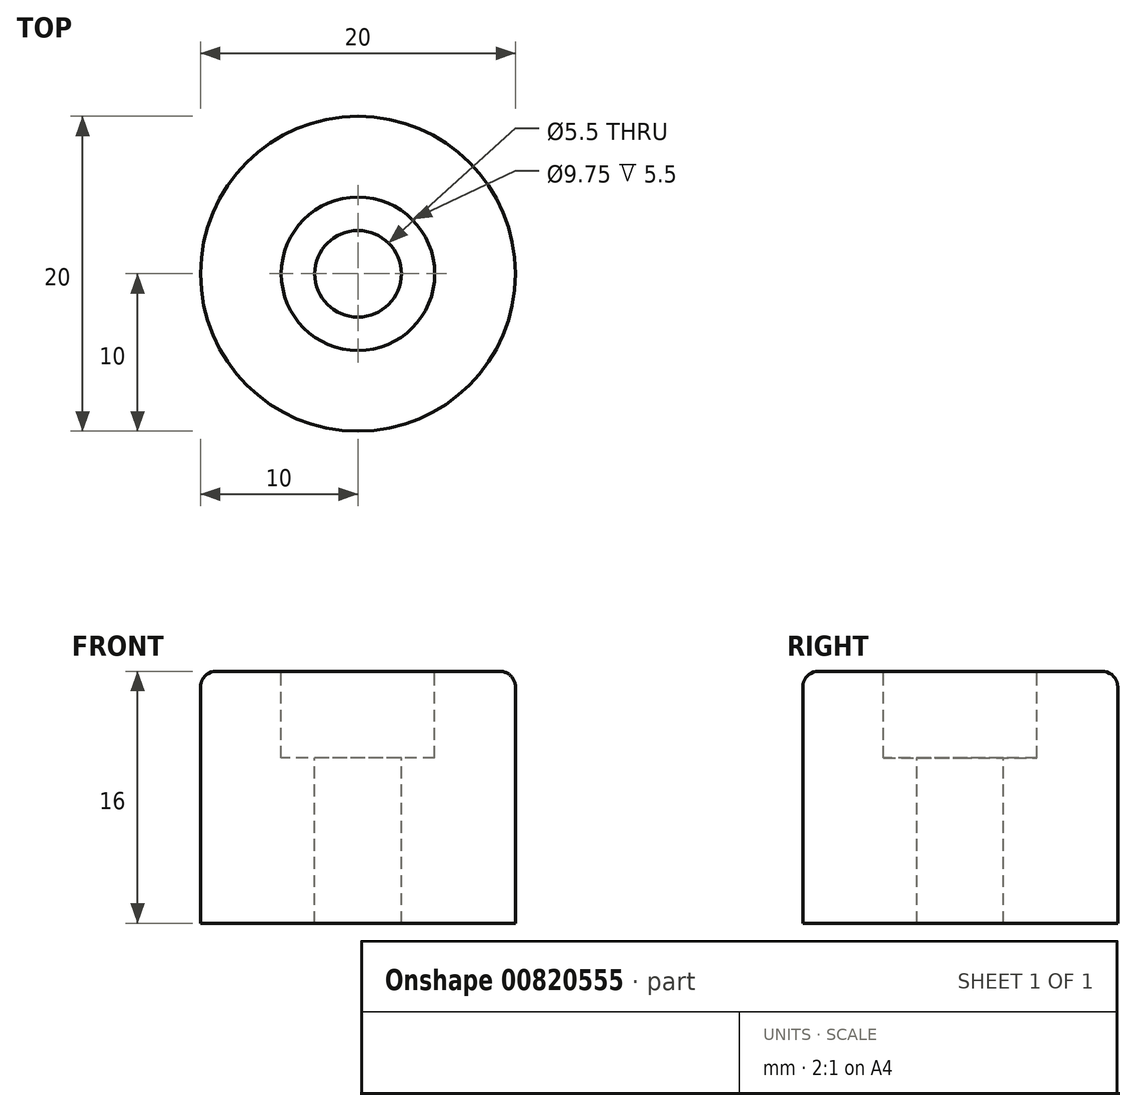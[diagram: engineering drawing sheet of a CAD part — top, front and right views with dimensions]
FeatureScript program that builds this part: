
annotation { "Feature Type Name" : "Feature", "Feature Type Description" : "" }
export const myFeature = defineFeature(function(context is Context, id is Id, definition is map)
    precondition{}
    {
        {
            var Q0;
            Q0=qCreatedBy(makeId("Top.planeOp"),FACE);
            var sketch = newSketch(context, id + "F0", { "sketchPlane" : qUnion([Q0])});
            skCircle(sketch, "E0", {"center": v(0, 0) * mm, "radius": 10 * mm});
            skSolve(sketch);
        }
        {
            var Q0;
            Q0=makeQuery(id+"F0.imprint","IMPRINT",FACE,{"disambiguationData":[TD([[makeQuery(id+"F0.imprint","IMPRINT",EDGE,{"derivedFrom":sQuery(id+"F0.wireOp",EDGE,"E0")}),1.0]])]});
            extrude(context, id + "F1", {"entities" : qUnion([Q0]), "depth" : 16 * mm, "offsetDistance" : 25 * mm});
        }
        {
            var Q0;
            Q0=makeQuery(id+"F1.opExtrude","CAP_FACE",FACE,{"disambiguationData":[OSD([sQuery(id+"F0.wireOp",EDGE,"E0")])],"isStart":false});
            var sketch = newSketch(context, id + "F2", { "sketchPlane" : qUnion([Q0])});
            skPoint(sketch, "E1", {"position": v(0, 0) * mm});
            skSolve(sketch);
        }
        {
            var Q0;
            Q0=sQuery(id+"F2.wireOp",VERTEX,"E1");
            var Q1;
            Q1=makeQuery(id+"F1.opExtrude","SWEPT_BODY",BODY,{"disambiguationData":[OSD([sQuery(id+"F0.wireOp",EDGE,"E0")])]});
            hole(context, id + "F3", {"style" : HoleStyle.C_BORE, "endStyle" : HoleEndStyle.THROUGH, "holeDiameter" : 5.5 * mm, "cBoreDiameter" : 9.75 * mm, "cBoreDepth" : 5.5 * mm, "majorDiameter" : 5 * mm, "isTappedThrough" : true, "tappedDepth" : 12 * mm, "tapClearance" : 3, "locations" : qUnion([Q0]), "scope" : qUnion([Q1])});
        }
        {
            var Q0;
            Q0=makeQuery(id+"F1.opExtrude","CAP_EDGE",EDGE,{"disambiguationData":[OSD([sQuery(id+"F0.wireOp",EDGE,"E0")])],"isStart":false});
            var Q1;
            Q1=makeQuery(id+"F3.hole-0.boolean.opBoolean","COPY",EDGE,{"derivedFrom":makeQuery(id+"F3.hole-0.opRevolve","SWEPT_EDGE",EDGE,{"disambiguationData":[OSD([sQuery(id+"F3.hole-0.sketch.wireOp",EDGE,"cbore_start_line_2"),sQuery(id+"F3.hole-0.sketch.wireOp",EDGE,"cbore_start_line_3")])]})});
            fillet(context, id + "F4", {"entities" : qUnion([Q0, Q1]), "radius" : 1 * mm, "tangentPropagation" : true, "allowEdgeOverflow" : false});
        }
    });
